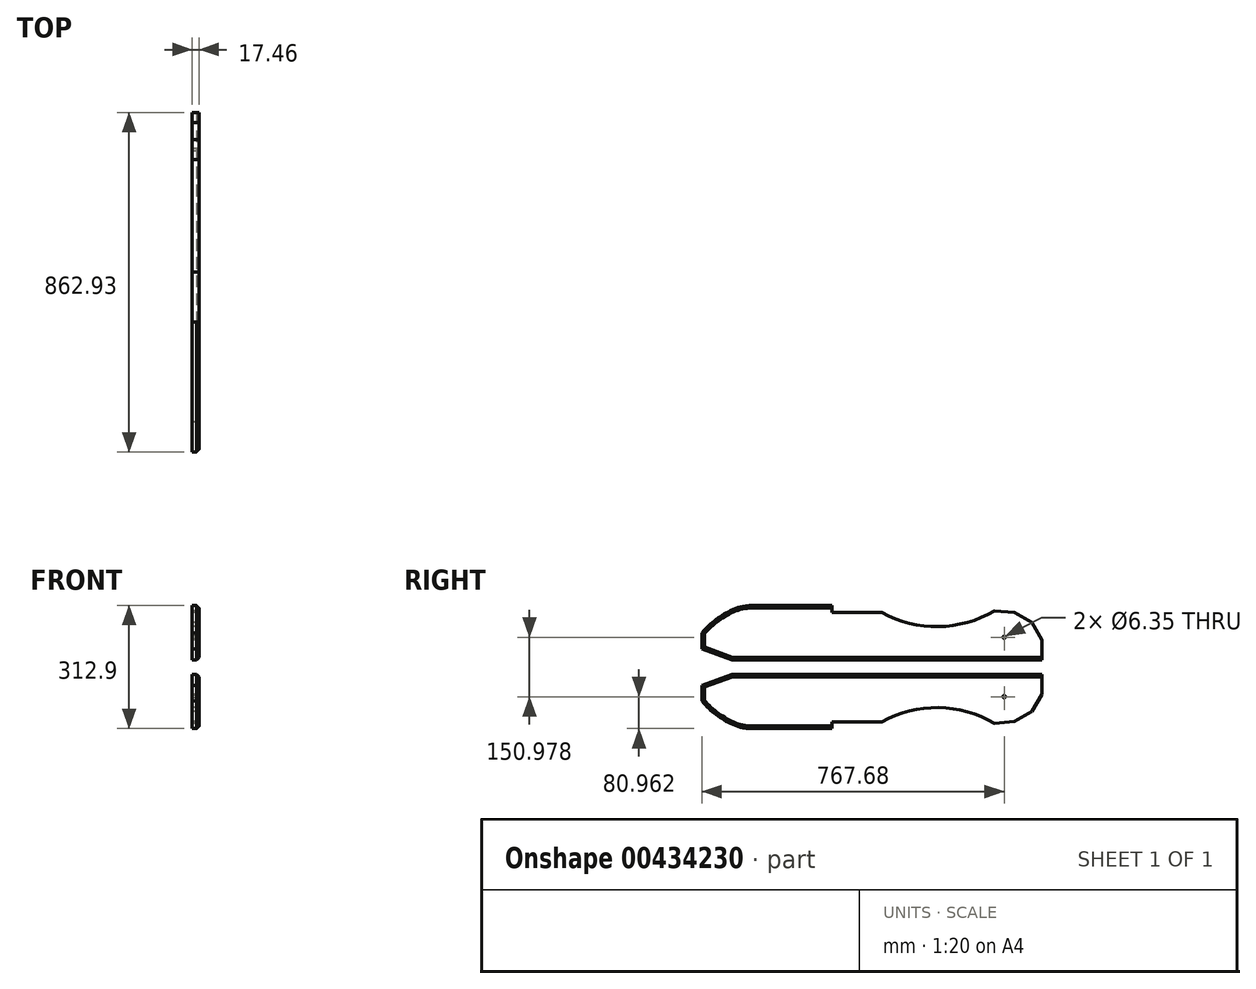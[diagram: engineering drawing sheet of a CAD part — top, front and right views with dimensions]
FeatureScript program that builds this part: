
annotation { "Feature Type Name" : "Feature", "Feature Type Description" : "" }
export const myFeature = defineFeature(function(context is Context, id is Id, definition is map)
    precondition{}
    {
        {
            var Q0;
            Q0=qCreatedBy(makeId("Right.planeOp"),FACE);
            var sketch = newSketch(context, id + "F0", { "sketchPlane" : qUnion([Q0])});
            skLineSegment(sketch, "E0", {"start": v(76.87, 0) * mm, "end": v(0.67, 27.73) * mm});
            skLineSegment(sketch, "E1", {"start": v(76.87, 0) * mm, "end": v(863.6, 0) * mm});
            skLineSegment(sketch, "E2", {"start": v(863.6, 50.8) * mm, "end": v(863.6, 0) * mm});
            skLineSegment(sketch, "E3", {"start": v(0.67, 27.73) * mm, "end": v(0.67, 68.26) * mm});
            skLineSegment(sketch, "E4", {"start": v(863.6, 50.8) * mm, "end": v(838.2, 94.8) * mm});
            skLineSegment(sketch, "E5", {"start": v(838.2, 94.8) * mm, "end": v(794.2, 120.2) * mm});
            skLineSegment(sketch, "E6", {"start": v(794.2, 120.2) * mm, "end": v(743.6, 124.62) * mm});
            skLineSegment(sketch, "E7", {"start": v(863.6, 50.8) * mm, "end": v(863.6, 113.04) * mm, "construction": true});
            skLineSegment(sketch, "E8", {"start": v(838.2, 94.8) * mm, "end": v(810.18, 143.32) * mm, "construction": true});
            skLineSegment(sketch, "E9", {"start": v(794.2, 120.2) * mm, "end": v(752.83, 144.08) * mm, "construction": true});
            skLineSegment(sketch, "E10", {"start": v(743.6, 124.62) * mm, "end": v(687.45, 129.53) * mm, "construction": true});
            skLineSegment(sketch, "E11", {"start": v(743.6, 124.62) * mm, "end": v(689.6, 110.15) * mm, "construction": true});
            skLineSegment(sketch, "E12", {"start": v(0.67, 68.26) * mm, "end": v(0.67, 138.11) * mm, "construction": true});
            skLineSegment(sketch, "E13", {"start": v(0.67, 138.11) * mm, "end": v(127.67, 138.11) * mm, "construction": true});
            skLineSegment(sketch, "E14", {"start": v(127.67, 138.11) * mm, "end": v(330.87, 138.11) * mm});
            skFitSpline(sketch, "E15", {"points": [v(127.67, 138.11) * mm, v(51.47, 112.71) * mm, v(0.67, 68.26) * mm], "startDerivative": vector(-186.22, 0) * mm, "endDerivative": vector(-96.54, -121.71) * mm});
            skLineSegment(sketch, "E16", {"start": v(330.87, 138.11) * mm, "end": v(330.87, 120.65) * mm});
            skLineSegment(sketch, "E17", {"start": v(330.87, 120.65) * mm, "end": v(457.87, 120.65) * mm});
            skLineSegment(sketch, "E18", {"start": v(457.87, 120.65) * mm, "end": v(743.6, 124.62) * mm, "construction": true});
            skPoint(sketch, "E19.startSnap0", {"position": v(600.73, 122.64) * mm});
            skArc(sketch, "E20", {"start": v(457.87, 120.65) * mm, "mid": v(601.26, 84.54) * mm, "end": v(743.6, 124.62) * mm});
            skLineSegment(sketch, "E21", {"start": v(457.87, 120.65) * mm, "end": v(569.63, 79.97) * mm, "construction": true});
            skLineSegment(sketch, "E22", {"start": v(600.73, 122.64) * mm, "end": v(600.73, 84.54) * mm, "construction": true});
            skLineSegment(sketch, "E23", {"start": v(-28.62, -18.34) * mm, "end": v(939.24, -18.34) * mm, "construction": true});
            skLineSegment(sketch, "E24.MirrorCS", {"start": v(76.87, -36.68) * mm, "end": v(863.6, -36.68) * mm});
            skLineSegment(sketch, "E25.MirrorCS", {"start": v(76.87, -36.68) * mm, "end": v(0.67, -64.41) * mm});
            skLineSegment(sketch, "E26.MirrorCS", {"start": v(0.67, -64.41) * mm, "end": v(0.67, -104.94) * mm});
            skFitSpline(sketch, "E27.MirrorCS", {"points": [v(127.67, -174.8) * mm, v(51.47, -149.4) * mm, v(0.67, -104.94) * mm], "startDerivative": vector(-186.22, 0) * mm, "endDerivative": vector(-96.54, 121.71) * mm});
            skLineSegment(sketch, "E28.MirrorCS", {"start": v(127.67, -174.8) * mm, "end": v(330.87, -174.8) * mm});
            skLineSegment(sketch, "E29.MirrorCS", {"start": v(330.87, -174.8) * mm, "end": v(330.87, -157.33) * mm});
            skLineSegment(sketch, "E30.MirrorCS", {"start": v(330.87, -157.33) * mm, "end": v(457.87, -157.33) * mm});
            skArc(sketch, "E31.MirrorCS", {"start": v(457.87, -157.33) * mm, "mid": v(601.26, -121.22) * mm, "end": v(743.6, -161.3) * mm});
            skLineSegment(sketch, "E32.MirrorCS", {"start": v(794.2, -156.87) * mm, "end": v(743.6, -161.3) * mm});
            skLineSegment(sketch, "E33.MirrorCS", {"start": v(863.6, -87.48) * mm, "end": v(863.6, -36.68) * mm});
            skLineSegment(sketch, "E34.MirrorCS", {"start": v(863.6, -87.48) * mm, "end": v(838.2, -131.47) * mm});
            skLineSegment(sketch, "E35.MirrorCS", {"start": v(838.2, -131.47) * mm, "end": v(794.2, -156.87) * mm});
            skCircle(sketch, "E36", {"center": v(768.35, 57.15) * mm, "radius": 3.18 * mm});
            skCircle(sketch, "E37.MirrorC", {"center": v(768.35, -93.83) * mm, "radius": 3.18 * mm});
            skSolve(sketch);
        }
        {
            var Q0;
            Q0 = qSketchRegion(id + "F0", true);
            extrude(context, id + "F1", {"entities" : qUnion([Q0]), "depth" : 17.46 * mm});
        }
        {
            var Q0;
            Q0=makeQuery(id+"F1.opExtrude","CAP_EDGE",EDGE,{"disambiguationData":[OSD([sQuery(id+"F0.wireOp",EDGE,"E0")])],"isStart":false});
            var Q1;
            Q1=makeQuery(id+"F1.opExtrude","CAP_EDGE",EDGE,{"disambiguationData":[OSD([sQuery(id+"F0.wireOp",EDGE,"E3")])],"isStart":false});
            var Q2;
            Q2=makeQuery(id+"F1.opExtrude","CAP_EDGE",EDGE,{"disambiguationData":[OSD([sQuery(id+"F0.wireOp",EDGE,"E15")])],"isStart":false});
            var Q3;
            Q3=makeQuery(id+"F1.opExtrude","CAP_EDGE",EDGE,{"disambiguationData":[OSD([sQuery(id+"F0.wireOp",EDGE,"E1")])],"isStart":false});
            var Q4;
            Q4=makeQuery(id+"F1.opExtrude","CAP_EDGE",EDGE,{"disambiguationData":[OSD([sQuery(id+"F0.wireOp",EDGE,"E24.MirrorCS")])],"isStart":false});
            var Q5;
            Q5=makeQuery(id+"F1.opExtrude","CAP_EDGE",EDGE,{"disambiguationData":[OSD([sQuery(id+"F0.wireOp",EDGE,"E25.MirrorCS")])],"isStart":false});
            var Q6;
            Q6=makeQuery(id+"F1.opExtrude","CAP_EDGE",EDGE,{"disambiguationData":[OSD([sQuery(id+"F0.wireOp",EDGE,"E26.MirrorCS")])],"isStart":false});
            var Q7;
            Q7=makeQuery(id+"F1.opExtrude","CAP_EDGE",EDGE,{"disambiguationData":[OSD([sQuery(id+"F0.wireOp",EDGE,"E27.MirrorCS")])],"isStart":false});
            chamfer(context, id + "F2", {"entities" : qUnion([Q0, Q1, Q2, Q3, Q4, Q5, Q6, Q7]), "width" : 6.35 * mm, "tangentPropagation" : true});
        }
    });
